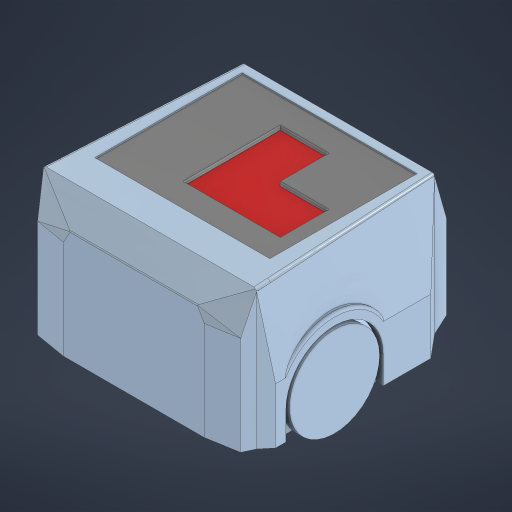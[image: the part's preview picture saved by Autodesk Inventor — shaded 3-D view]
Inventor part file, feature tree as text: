
AUTODESK INVENTOR PART (.ipt)
format: ipt  version: 2024 (Build 280153000, 153)  size: 2,238,976 bytes
history: native  units: mm
features: other x56, sketch x42, extrude x40, loft x18, fillet x8, plane x1
ambient origin geometry x8: Origin, YZ Plane, XZ Plane, XY Plane, X Axis, Y Axis, Z Axis, Center Point
bodies: Body1 (feature_tree), Body2 (feature_tree)
feature tree (165):
  other  "Sólido1"
  extrude  "Base"  Depth=10.0mm TaperAngle=0.0deg
  extrude  "Llantas"  Depth=70.0mm
  extrude  "Carroceria"  Depth=75.0mm
  extrude  "Extrusión30"  Depth=150.0mm
  extrude  "Extrusión31"  Depth=10.0mm TaperAngle=0.0deg
  extrude  "Extrusión32"  Depth=8.726646mm
  extrude  "Extrusión33"  Depth=40.0mm
  extrude  "Extrusión34"  Depth=15.0mm
  extrude  "Extrusión35"  Depth=50.0mm
  extrude  "Extrusión38"  Depth=11.34464mm
  extrude  "Extrusión39"  Depth=5.0mm
  extrude  "Extrusión100"  Depth=3.0mm
  extrude  "Extrusión102"  Depth=5.0mm
  extrude  "Extrusión103"  Depth=3.0mm
  extrude  "Extrusión104"  TaperAngle=0.0deg  [1 undecoded]
  loft  "Solevación32"
  loft  "Solevación33"
  extrude  "Extrusión43"  TaperAngle=0.0deg  [1 undecoded]
  extrude  "Extrusión96"  Depth=3.0mm
  extrude  "Extrusión110"  Depth=3.0mm
  extrude  "Extrusión90"  Depth=3.0mm
  extrude  "Extrusión94"  Depth=3.0mm
  extrude  "Extrusión95"  Depth=3.0mm
  loft  "Solevación10"
  loft  "Solevación11"
  extrude  "Extrusión53"  TaperAngle=0.0deg  [1 undecoded]
  extrude  "Extrusión93"  TaperAngle=0.0deg  [1 undecoded]
  loft  "Solevación8"
  loft  "Solevación9"
  extrude  "Extrusión84"  Depth=80.0mm TaperAngle=0.0deg
  extrude  "Extrusión64"  Depth=5.0mm
  extrude  "Extrusión65"  Depth=5.0mm TaperAngle=0.0deg
  extrude  "Extrusión67"  Depth=5.0mm TaperAngle=0.0deg
  extrude  "Extrusión111"  Depth=6.0mm
  plane  "Plano de trabajo5"
  extrude  "Extrusión98"  Depth=3.0mm
  loft  "Solevación18"
  loft  "Solevación19"
  loft  "Solevación20"
  loft  "Solevación21"
  loft  "Solevación22"
  loft  "Solevación23"
  loft  "Solevación24"
  loft  "Solevación30"
  loft  "Solevación26"
  loft  "Solevación31"
  loft  "Solevación34"
  loft  "Solevación35"
  fillet  "Empalme1"  Radius=100.0mm
  fillet  "Empalme2"  [1 undecoded]
  fillet  "Empalme3"  Radius=30.0mm
  fillet  "Empalme4"  Radius=10.0mm
  fillet  "Empalme5"  Radius=11.34464mm
  fillet  "Empalme6"  Radius=10.0mm
  fillet  "Empalme7"  Radius=11.34464mm
  extrude  "Extrusión105"  TaperAngle=0.0deg  [1 undecoded]
  extrude  "Extrusión106"  Depth=10.0mm TaperAngle=0.0deg
  extrude  "Extrusión107"  Depth=12.0mm
  extrude  "Extrusión108"  Depth=10.0mm
  extrude  "Extrusión109"  Depth=12.0mm TaperAngle=0.0deg
  extrude  "Extrusión112"  TaperAngle=0.0deg  [1 undecoded]
  extrude  "Extrusión113"  Depth=12.0mm
  extrude  "Extrusión114"  Depth=12.0mm
  extrude  "Extrusión115"  Depth=12.0mm
  extrude  "Extrusión116"  Depth=12.0mm
  extrude  "Extrusión117"  Depth=12.0mm TaperAngle=0.0deg
  fillet  "Empalme8"  Radius=5.0mm
  sketch  "Boceto Base"  dims[d424=37.5mm d425=5.0mm]
  sketch  "Boceto Llantas"  dims[d426=5.0mm d427=5.0mm]
  sketch  "Boceto Carroceria"  dims[d428=5.0mm d429=15.0mm d430=0.0mm d431=10.0mm d432=5.0mm d433=85.592mm d434=0.0mm d439=10.0mm d440=0.0mm d494=10.0mm d495=0.0mm d514=100.0mm d515=0.0mm d530=30.0deg d531=30.0mm d532=10.0mm d533=0.0mm d534=0.0mm d535=90.0deg d536=0.0mm d537=90.0deg d538=0.0mm d539=90.0deg d540=0.0mm d541=90.0deg d542=11.34464mm d543=10.0mm d544=0.0mm d545=11.34464mm d546=0.0mm d547=10.0mm d548=0.0mm d549=5.0mm d550=10.0mm d551=105.0mm d552=0.0mm d553=0.0mm d554=90.0deg d559=0.0mm d560=90.0deg d595=20.0mm d596=20.0mm d597=30.0mm d598=30.0mm d599=5.0mm d600=0.0mm d611=5.0mm d612=0.0mm d613=90.0deg d614=0.0mm d615=90.0deg d616=0.0mm d617=90.0deg d618=0.0mm d619=90.0deg d620=0.0mm d621=90.0deg d622=0.0mm d623=90.0deg d624=0.0mm d625=90.0deg d626=0.0mm d627=90.0deg d628=0.0mm d629=90.0deg d630=0.0mm d631=90.0deg d632=5.0mm d633=0.0mm d634=90.0deg d635=0.0mm d636=90.0deg d637=0.0mm d638=90.0deg d639=0.0mm d640=90.0deg d645=0.0mm d646=90.0deg d647=0.0mm d648=90.0deg d653=20.0mm d654=85.0mm d655=42.5mm d656=70.0mm d657=200.0mm d658=0.0mm d669=40.0mm d670=0.0mm d671=0.0mm d672=90.0deg d673=0.0mm d674=90.0deg d676=0.0mm d677=90.0deg d680=0.0mm d681=90.0deg d684=5.0mm d685=0.0mm d686=5.0mm d687=0.0mm d688=0.0mm d689=90.0deg d690=0.0mm d691=90.0deg d692=0.0mm d693=90.0deg d694=0.0mm d695=90.0deg d697=0.0mm d698=90.0deg d699=0.0mm d700=90.0deg d701=0.0mm d702=90.0deg d703=0.0mm d704=90.0deg d705=2.0mm d706=2.0mm d707=2.0mm d708=2.0mm d709=2.0mm d710=2.0mm d711=2.0mm d712=100.0mm d713=0.0mm d714=100.0mm d715=0.0mm d716=10.0mm d717=15.0mm d718=10.0mm d719=10.0mm d720=15.0mm d723=10.0mm d724=10.0mm d725=3.0mm d726=5.0mm d727=5.0mm d728=3.0mm d729=5.0mm d730=5.0mm d731=5.0mm d732=0.0mm d733=5.0mm d734=10.0mm d735=0.0mm d737=5.0mm d738=10.0mm d739=0.0mm d740=3.0mm d741=120.0deg d742=120.0deg d743=3.0mm d744=120.0deg d745=3.0mm d746=120.0deg d747=2.598mm d748=5.196152mm d749=3.0mm d750=2.0mm d751=0.0mm d752=3.0mm d753=3.0mm d754=120.0deg d755=3.0mm d756=120.0deg d757=3.0mm d758=3.0mm d759=120.0deg d760=3.0mm d761=2.598mm d762=2.0mm d763=0.0mm d764=0.0mm d765=90.0deg d766=0.0mm d767=90.0deg d768=10.0mm d769=0.0mm d770=1.0mm d771=0.0mm d772=10.5mm d773=18.0mm d774=35.0mm d775=35.0mm d776=35.0mm d777=70.0mm d778=3.0mm d779=0.0mm d783=65.0mm d784=0.0mm d785=5.0mm d786=0.0mm d787=0.0mm d788=35.0mm d789=65.0mm d790=5.0mm d791=0.0mm d792=30.0mm d793=12.5mm d794=0.0mm d795=12.0mm d64=0.5mm d65=0.872665mm d66=0.5mm d67=0.872665mm d229=0.5mm d230=0.872665mm d231=0.5mm d232=0.872665mm d284=0.5mm d285=0.872665mm d286=0.5mm d287=0.872665mm d288=0.5mm d289=0.872665mm d290=0.5mm d342=0.5mm d343=0.872665mm d344=0.5mm d345=0.872665mm d352=0.5mm d353=0.872665mm d354=0.5mm d355=0.872665mm d364=0.5mm d365=0.872665mm d366=0.5mm d367=0.872665mm d386=0.5mm d387=0.872665mm d388=0.5mm d389=0.872665mm d472=0.5mm d473=0.872665mm d474=0.5mm d475=0.872665mm d525=0.5mm d526=0.872665mm d527=0.5mm d528=0.872665mm]
  sketch  "Boceto28"  dims[d0=160.0mm d2=10.0mm d3=0.0mm]
  sketch  "Boceto30"  dims[d4=70.0mm d5=70.0mm]
  sketch  "Boceto31"  dims[d6=20.0mm d7=75.0mm]
  sketch  "Boceto32"  dims[d8=80.0mm d9=150.0mm]
  sketch  "Boceto33"  dims[d10=25.0mm d11=10.0mm d12=0.0mm]
  sketch  "Boceto34"  dims[d13=30.0mm d14=8.726646mm]
  sketch  "Boceto37"  dims[d15=11.34464mm d16=40.0mm]
  sketch  "Boceto38"  dims[d17=15.0mm d18=15.0mm]
  sketch  "Boceto43"  dims[d19=6.0mm d20=50.0mm]
  sketch  "Boceto54"  dims[d21=8.726646mm d22=11.34464mm]
  sketch  "Boceto64"  dims[d23=6.0mm d24=5.0mm]
  sketch  "Boceto65"  dims[d25=10.0mm d26=0.0mm d291=3.0mm]
  sketch  "Boceto67"  dims[d292=5.0mm d293=5.0mm]
  sketch  "Boceto106"  dims[d294=3.0mm d295=5.0mm]
  sketch  "Boceto114"  dims[d297=3.0mm d298=0.0mm]
  sketch  "Boceto117"  dims[d299=0.0mm d300=0.0mm]
  sketch  "Boceto118"  dims[d301=0.0mm d303=5.0mm]
  sketch  "Boceto119"  dims[d304=3.0mm d305=0.0mm]
  sketch  "Boceto120"  dims[d306=5.0mm d307=3.0mm]
  sketch  "Boceto125"  dims[d308=5.0mm d309=3.0mm]
  sketch  "Boceto129"  dims[d310=5.0mm d311=3.0mm]
  other  "Aristas31"
  other  "Aristas32"
  other  "Aristas33"
  other  "Aristas34"
  other  "Aristas35"
  other  "Aristas36"
  other  "Aristas37"
  other  "Aristas38"
  other  "Aristas39"
  sketch  "Boceto131"  dims[d312=5.0mm d313=3.0mm]
  other  "Aristas40"
  other  "Aristas47"
  other  "Aristas48"
  other  "Sólido8"
  other  "Aristas49"
  other  "Aristas50"
  sketch  "Boceto132"  dims[d314=3.0mm d315=5.0mm]
  sketch  "Boceto135"  dims[d316=0.0mm d317=0.0mm]
  other  "Aristas57"
  other  "Aristas58"
  other  "Aristas59"
  other  "Aristas60"
  sketch  "Boceto138"  dims[d318=0.0mm d319=0.0mm]
  sketch  "Boceto139"  dims[d320=0.0mm d321=0.0mm]
  other  "Aristas65"
  other  "Aristas66"
  other  "Aristas67"
  other  "Aristas68"
  other  "Aristas69"
  other  "Aristas70"
  other  "Aristas71"
  other  "Aristas72"
  sketch  "Boceto142"  dims[d322=0.0mm d323=0.0mm]
  sketch  "Boceto143"  dims[d324=0.0mm d325=0.0mm]
  sketch  "Boceto144"  dims[d326=0.0mm d327=0.1mm d328=0.0mm]
  sketch  "Boceto145"  dims[d329=0.0mm d330=80.0mm d331=0.0mm]
  sketch  "Boceto146"  dims[d332=71.0mm d333=0.0mm d334=5.0mm]
  sketch  "Boceto148"  dims[d335=5.0mm d336=5.0mm d337=0.0mm]
  other  "Aristas73"
  other  "Aristas74"
  other  "Aristas75"
  other  "Aristas76"
  sketch  "Boceto149"  dims[d338=100.0mm d339=0.0mm d340=5.0mm d341=0.0mm]
  other  "Aristas77"
  other  "Aristas78"
  other  "Aristas79"
  other  "Aristas80"
  sketch  "Boceto150"  dims[d346=5.0mm d347=0.0mm d348=6.0mm]
  sketch  "Boceto152"  dims[d349=70.0mm d350=0.0mm d368=3.0mm]
  sketch  "Boceto153"  dims[d369=5.0mm d370=47.5mm]
  sketch  "Boceto154"  dims[d371=5.0mm d372=5.0mm]
  sketch  "Boceto155"  dims[d373=5.0mm d374=15.0mm d375=0.0mm]
  sketch  "Boceto156"  dims[d396=70.0mm d397=0.0mm d422=3.0mm]
  other  "Finish1"
  other  "Finish2"
  other  "Finish3"
  other  "Finish4"
  other  "Finish5"
  other  "Finish6"
  other  "Finish7"
  other  "Finish8"
  other  "Finish9"
  other  "Finish10"
  other  "Finish11"
  other  "Finish12"
  other  "Finish13"
  other  "Finish14"
  other  "Finish15"
  other  "Finish16"
  other  "Finish17"
  other  "Finish18"
  other  "Finish19"
  other  "Finish20"
note: 7 required parameter values undecoded (feature->parameter linkage not recoverable at this tier; creation-order binding heuristic only, values carry confidence <= 0.55)
